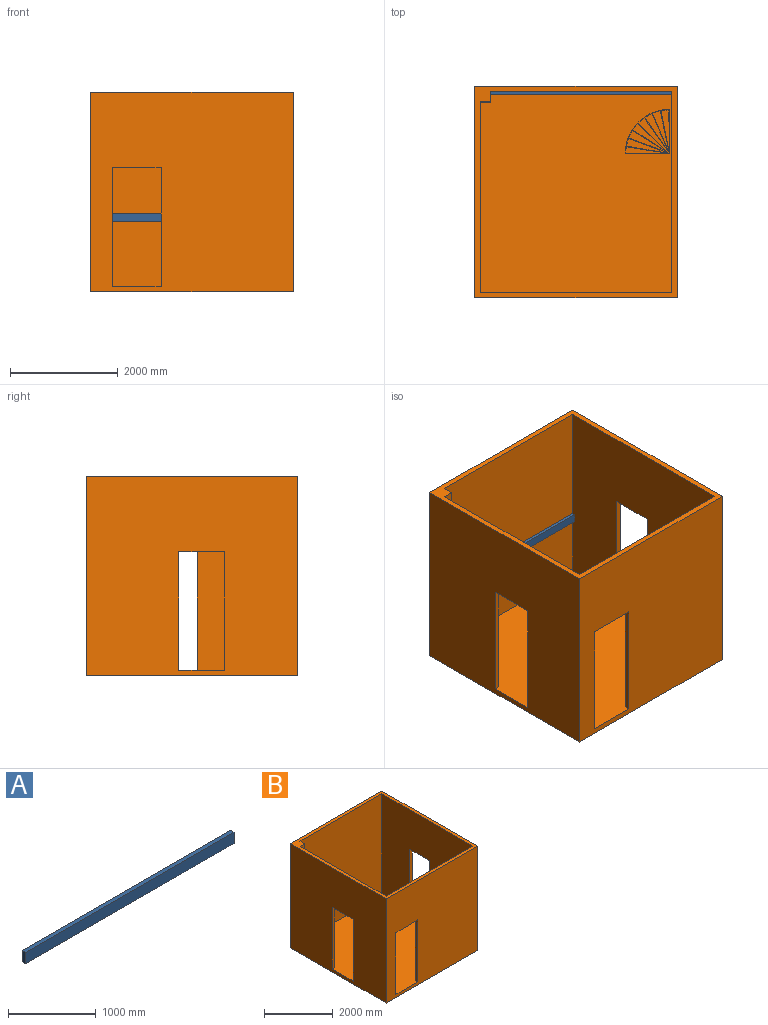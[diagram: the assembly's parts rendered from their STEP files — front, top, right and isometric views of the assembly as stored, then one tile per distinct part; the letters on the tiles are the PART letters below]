
ASSEMBLY  parts=2 mates=1
PART A: 6 faces, bbox 3360x60x155 mm
  f0: plane 155x60mm, normal (1,0,0), area 9300mm2, adj f1,f3,f4,f5
  f1: plane 3360x60mm, normal (0,0,1), area 201600mm2, adj f0,f2,f4,f5
  f2: plane 155x60mm, normal (-1,0,0), area 9300mm2, adj f1,f3,f4,f5
  f3: plane 3360x60mm, normal (0,0,-1), area 201600mm2, adj f0,f2,f4,f5
  f4: plane 3360x155mm, normal (0,-1,0), area 520800mm2, adj f0,f1,f2,f3
  f5: plane 3360x155mm, normal (0,1,0), area 520800mm2, adj f0,f1,f2,f3
PART B: 70 faces, bbox 3746x3920x3700 mm
  f0: plane 3600x3526mm, normal (1,0,0), area 10819200mm2, adj f4,f9,f10,f11,f67,f68,f69
  f1: plane 3920x3700mm, normal (-1,0,0), area 12629600mm2, adj f3,f4,f6,f11,f12,f67,f68,f69
  f2: plane 3720x3600mm, normal (-1,0,0), area 11614400mm2, adj f4,f8,f9,f11,f64,f65,f66
  f3: plane 3746x3700mm, normal (0,-1,0), area 11880200mm2, adj f1,f4,f5,f11,f12,f61,f62,f63
  f4: plane 3820x3746mm, normal (0,0,1), area 12882933.9mm2, adj f0,f1,f2,f3,f5,f7,f8,f9
  f5: plane 3920x3700mm, normal (1,0,0), area 12726400mm2, adj f3,f4,f6,f11,f12,f64,f65,f66
  f6: plane 3746x3700mm, normal (0,1,0), area 13860200mm2, adj f1,f5,f11,f12
  f7: plane 3600x194mm, normal (1,0,0), area 698400mm2, adj f4,f8,f10,f11
  f8: plane 3600x3360mm, normal (0,-1,0), area 12096000mm2, adj f2,f4,f7,f11
  f9: plane 3600x3546mm, normal (0,1,0), area 10785600mm2, adj f0,f2,f4,f11,f61,f62,f63
  f10: plane 3600x186mm, normal (0,-1,0), area 669600mm2, adj f0,f4,f7,f11
  f11: plane 3920x3746mm, normal (0,0,1), area 1529284mm2, adj f0,f1,f2,f3,f5,f6,f7,f8
  f12: plane 3920x3746mm, normal (0,0,-1), area 14684320mm2, adj f1,f3,f5,f6
  f13: plane 523.43x10mm, normal (1,0,0), area 5234.3mm2, adj f14,f51,f52,f60
  f14: plane 744.47x150.5mm, normal (-0.98,-0.2,0), area 7595.3mm2, adj f13,f15,f52,f60
  f15: cylinder r=810mm len=146.36mm, axis (0,0,1), area 1474.3mm2, adj f14,f51,f52,f60
  f16: plane 745.64x164.33mm, normal (0.98,0.22,0), area 7635.4mm2, adj f17,f43,f52,f59
  f17: plane 21.65x10mm, normal (1,0,0), area 216.5mm2, adj f16,f18,f52,f59
  f18: plane 722.67x304.63mm, normal (-0.92,-0.39,0), area 7842.6mm2, adj f17,f43,f52,f59
  f19: plane 718.18x317.61mm, normal (0.91,0.4,0), area 7852.8mm2, adj f20,f44,f52,f58
  f20: plane 10x7.94mm, normal (1,0,0), area 79.4mm2, adj f19,f21,f52,f58
  f21: plane 654.59x446.29mm, normal (-0.83,-0.56,0), area 7922.5mm2, adj f20,f44,f52,f58
  f22: plane 10x4.87mm, normal (0,-1,0), area 48.7mm2, adj f23,f45,f52,f57
  f23: plane 664.94x429.46mm, normal (-0.54,-0.84,0), area 7915.7mm2, adj f22,f24,f52,f57
  f24: cylinder r=810mm len=115.9mm, axis (0,0,1), area 1474.3mm2, adj f23,f45,f52,f57
  f25: plane 10x9.39mm, normal (0,-1,0), area 93.9mm2, adj f26,f46,f52,f56
  f26: plane 728.53x285.93mm, normal (-0.37,-0.93,0), area 7826.3mm2, adj f25,f27,f52,f56
  f27: cylinder r=810mm len=131.59mm, axis (0,0,1), area 1474.3mm2, adj f26,f46,f52,f56
  f28: plane 29.86x10mm, normal (0,-1,0), area 298.6mm2, adj f29,f47,f52,f55
  f29: plane 740.98x130.66mm, normal (-0.17,-0.98,0), area 7524.1mm2, adj f28,f30,f52,f55
  f30: cylinder r=810mm len=142.07mm, axis (0,0,1), area 1474.3mm2, adj f29,f47,f52,f55
  f31: plane 746.8x10mm, normal (0,-1,0), area 7468mm2, adj f32,f48,f52,f54
  f32: cylinder r=810mm len=116.71mm, axis (0,0,1), area 1172.3mm2, adj f31,f48,f52,f54
  f33: plane 10x4.13mm, normal (1,0,0), area 41.3mm2, adj f34,f49,f52,f53
  f34: plane 10x0.25mm, normal (0,-1,0), area 2.5mm2, adj f33,f35,f52,f53
  f35: plane 569.6x555.57mm, normal (-0.7,-0.72,0), area 7956.8mm2, adj f34,f36,f52,f53
  f36: cylinder r=810mm len=111.95mm, axis (0,0,1), area 1474.3mm2, adj f35,f49,f52,f53
  f37: plane 10x0.06mm, normal (1,0,0), area 0.6mm2, adj f4,f38,f50,f52
  f38: cylinder r=820mm len=809.94mm, axis (0,0,1), area 12680.5mm2, adj f4,f37,f39,f52
  f39: plane 10x0.06mm, normal (0,-1,0), area 0.6mm2, adj f4,f38,f40,f52
  f40: plane 10x10mm, normal (1,0,0), area 100mm2, adj f4,f39,f41,f52
  f41: plane 820x10mm, normal (0,1,0), area 8200mm2, adj f4,f40,f42,f52
  f42: plane 820x10mm, normal (-1,0,0), area 8200mm2, adj f4,f41,f50,f52
  f43: cylinder r=810mm len=140.3mm, axis (0,0,1), area 1474.3mm2, adj f16,f18,f52,f59
  f44: cylinder r=810mm len=128.68mm, axis (0,0,1), area 1474.3mm2, adj f19,f21,f52,f58
  f45: plane 579.02x545.37mm, normal (0.69,0.73,0), area 7954.2mm2, adj f22,f24,f52,f57
  f46: plane 671.89x417.52mm, normal (0.53,0.85,0), area 7910.5mm2, adj f25,f27,f52,f56
  f47: plane 732.21x272.72mm, normal (0.35,0.94,0), area 7813.5mm2, adj f28,f30,f52,f55
  f48: plane 736.89x116.71mm, normal (0.16,0.99,0), area 7460.8mm2, adj f31,f32,f52,f54
  f49: plane 647.06x457.9mm, normal (0.82,0.58,0), area 7926.9mm2, adj f33,f36,f52,f53
  f50: plane 10x10mm, normal (0,-1,0), area 100mm2, adj f4,f37,f42,f52
  f51: plane 236.98x10mm, normal (1,0.02,0), area 2370.1mm2, adj f13,f15,f52,f60
  f52: plane 820x820mm, normal (0,0,1), area 69398.6mm2, adj f13,f14,f15,f16,f17,f18,f19,f20
  f53: plane 651.19x569.85mm, normal (0,0,1), area 59687.4mm2, adj f33,f34,f35,f36,f49
  f54: plane 746.8x116.71mm, normal (0,0,1), area 43745.9mm2, adj f31,f32,f48
  f55: plane 770.85x272.72mm, normal (0,0,1), area 59560mm2, adj f28,f29,f30,f47
  f56: plane 737.92x417.52mm, normal (0,0,1), area 59662.4mm2, adj f25,f26,f27,f46
  f57: plane 669.8x545.37mm, normal (0,0,1), area 59685mm2, adj f22,f23,f24,f45
  f58: plane 726.12x446.29mm, normal (0,0,1), area 59669.6mm2, adj f19,f20,f21,f44
  f59: plane 767.3x304.63mm, normal (0,0,1), area 59601.1mm2, adj f16,f17,f18,f43
  f60: plane 760.41x150.5mm, normal (0,0,1), area 57092.2mm2, adj f13,f14,f15,f51
  f61: plane 2200x100mm, normal (1,0,0), area 220000mm2, adj f3,f4,f9,f63
  f62: plane 2200x100mm, normal (-1,0,0), area 220000mm2, adj f3,f4,f9,f63
  f63: plane 900x100mm, normal (0,0,-1), area 90000mm2, adj f3,f9,f61,f62
  f64: plane 2200x100mm, normal (0,1,0), area 220000mm2, adj f2,f4,f5,f65
  f65: plane 808x100mm, normal (0,0,-1), area 80800mm2, adj f2,f5,f64,f66
  f66: plane 2200x100mm, normal (0,-1,0), area 220000mm2, adj f2,f4,f5,f65
  f67: plane 2200x100mm, normal (0,-1,0), area 220000mm2, adj f0,f1,f4,f68
  f68: plane 852x100mm, normal (0,0,-1), area 85200mm2, adj f0,f1,f67,f69
  f69: plane 2200x100mm, normal (0,1,0), area 220000mm2, adj f0,f1,f4,f68
PLACE A t=(-3076.1,2340.61,1914.15)mm
PLACE B t=(-3169.1,480.61,636.65)mm
MATE fastened A.f5 <-> B.f8  axis (0,1,0) through (-3076.1,2340.61,1914.15)mm
